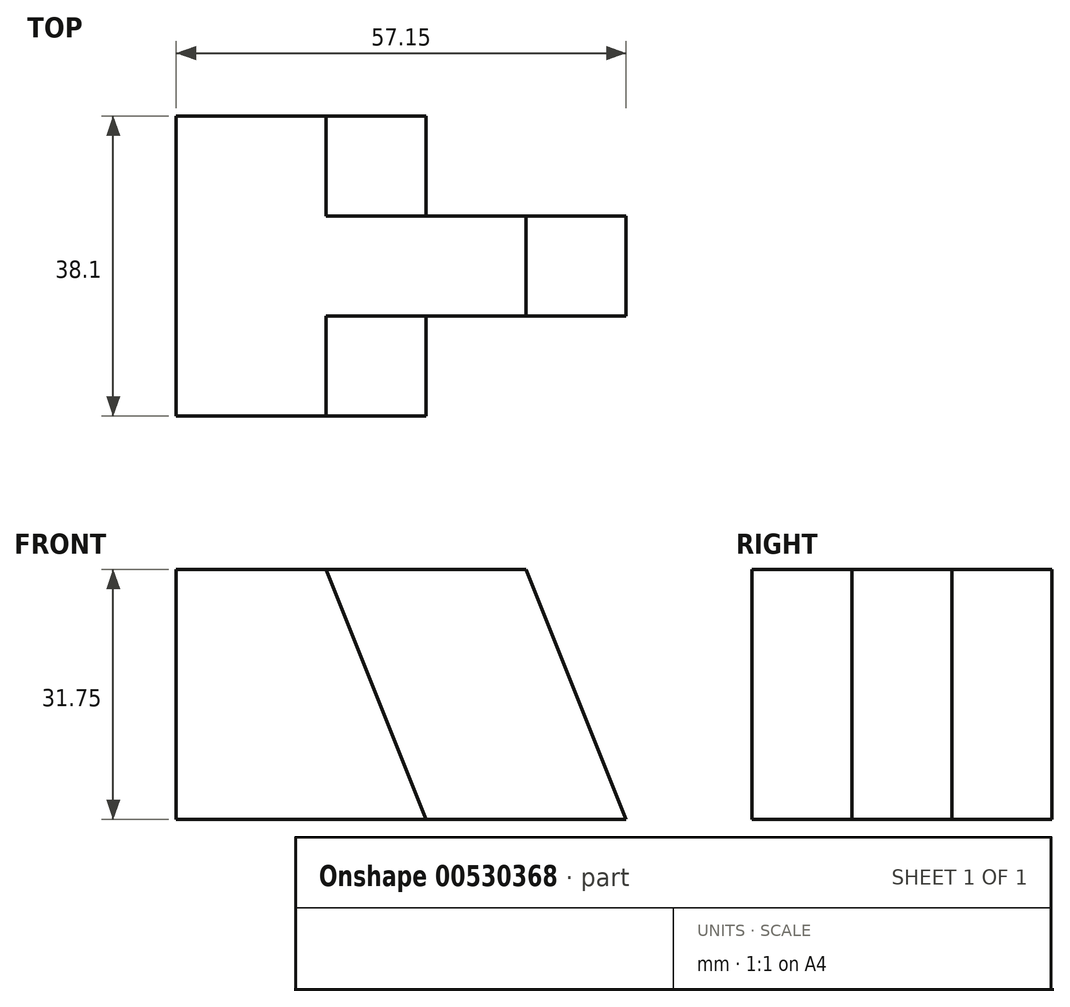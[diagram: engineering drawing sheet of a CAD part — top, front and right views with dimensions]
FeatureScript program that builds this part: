
annotation { "Feature Type Name" : "Feature", "Feature Type Description" : "" }
export const myFeature = defineFeature(function(context is Context, id is Id, definition is map)
    precondition{}
    {
        {
            var Q0;
            Q0=qCreatedBy(makeId("Top.planeOp"),FACE);
            var sketch = newSketch(context, id + "F0", { "sketchPlane" : qUnion([Q0])});
            skLineSegment(sketch, "E0", {"start": v(-57.15, 0) * mm, "end": v(-57.15, 38.1) * mm});
            skLineSegment(sketch, "E1", {"start": v(-57.15, 38.1) * mm, "end": v(-25.4, 38.1) * mm});
            skLineSegment(sketch, "E2", {"start": v(-25.4, 38.1) * mm, "end": v(-25.4, 25.4) * mm});
            skLineSegment(sketch, "E3", {"start": v(-25.4, 25.4) * mm, "end": v(0, 25.4) * mm});
            skLineSegment(sketch, "E4", {"start": v(0, 25.4) * mm, "end": v(0, 12.7) * mm});
            skLineSegment(sketch, "E5", {"start": v(0, 12.7) * mm, "end": v(-25.4, 12.7) * mm});
            skLineSegment(sketch, "E6", {"start": v(-25.4, 12.7) * mm, "end": v(-25.4, 0) * mm});
            skLineSegment(sketch, "E7", {"start": v(-25.4, 0) * mm, "end": v(-57.15, 0) * mm});
            skSolve(sketch);
        }
        {
            var Q0;
            Q0 = qSketchRegion(id + "F0", true);
            extrude(context, id + "F1", {"entities" : qUnion([Q0]), "depth" : 31.75 * mm, "offsetDistance" : 25.4 * mm});
        }
        {
            var Q0;
            Q0=qCreatedBy(makeId("Front.planeOp"),FACE);
            var sketch = newSketch(context, id + "F2", { "sketchPlane" : qUnion([Q0])});
            skLineSegment(sketch, "E8", {"start": v(-12.7, 31.75) * mm, "end": v(0, 31.75) * mm});
            skLineSegment(sketch, "E9", {"start": v(0, 31.75) * mm, "end": v(0, 0) * mm});
            skLineSegment(sketch, "E10", {"start": v(0, 0) * mm, "end": v(-12.7, 31.75) * mm});
            skSolve(sketch);
        }
        {
            var Q0;
            Q0 = qSketchRegion(id + "F2", true);
            extrude(context, id + "F3", {"entities" : qUnion([Q0]), "operationType" : NewBodyOperationType.REMOVE, "oppositeDirection" : true, "depth" : 25.4 * mm, "offsetDistance" : 25.4 * mm});
        }
        {
            var Q0;
            Q0=qCreatedBy(makeId("Front.planeOp"),FACE);
            var sketch = newSketch(context, id + "F4", { "sketchPlane" : qUnion([Q0])});
            skLineSegment(sketch, "E11", {"start": v(-38.1, 31.75) * mm, "end": v(-25.4, 31.75) * mm});
            skLineSegment(sketch, "E12", {"start": v(-25.4, 31.75) * mm, "end": v(-25.4, 0) * mm});
            skLineSegment(sketch, "E13", {"start": v(-25.4, 0) * mm, "end": v(-38.1, 31.75) * mm});
            skSolve(sketch);
        }
        {
            var Q0;
            Q0 = qSketchRegion(id + "F4", true);
            extrude(context, id + "F5", {"entities" : qUnion([Q0]), "operationType" : NewBodyOperationType.REMOVE, "oppositeDirection" : true, "depth" : 12.7 * mm, "offsetDistance" : 25.4 * mm});
        }
        {
            var Q0;
            Q0=makeQuery(id+"F1.opExtrude","SWEPT_FACE",FACE,{"disambiguationData":[OSD([sQuery(id+"F0.wireOp",EDGE,"E1")])]});
            var sketch = newSketch(context, id + "F6", { "sketchPlane" : qUnion([Q0])});
            skLineSegment(sketch, "E14", {"start": v(25.4, 0) * mm, "end": v(25.4, 31.75) * mm});
            skLineSegment(sketch, "E15", {"start": v(25.4, 31.75) * mm, "end": v(38.1, 31.75) * mm});
            skLineSegment(sketch, "E16", {"start": v(38.1, 31.75) * mm, "end": v(25.4, 0) * mm});
            skSolve(sketch);
        }
        {
            var Q0;
            Q0 = qSketchRegion(id + "F6", true);
            extrude(context, id + "F7", {"entities" : qUnion([Q0]), "operationType" : NewBodyOperationType.REMOVE, "oppositeDirection" : true, "depth" : 12.7 * mm, "offsetDistance" : 25.4 * mm});
        }
    });
